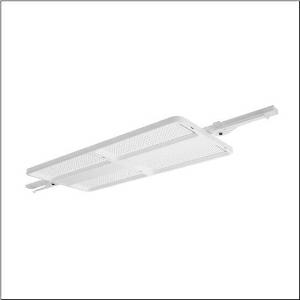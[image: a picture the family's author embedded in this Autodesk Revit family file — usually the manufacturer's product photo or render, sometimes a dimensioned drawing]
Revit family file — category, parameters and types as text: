
# Revit family: highbay_11_fur_modario_r__tragschiene_maxi_51hn11db4rma_e5d8
name_source: partatom
category: Lighting Fixtures
units: mm (PartAtom-declared; Revit-internal decimal feet)

## family parameters
Cut with Voids When Loaded = No
Host = Face
Light Source = No
Part Type = Normal
Room Calculation Point = No
Round Connector Dimension = Use Diameter
Shared = No

## types (1)
- --- (1 x LED, 42500 lm, 213.7 W, 4000K)
    Apparent Load = 214 VA
    CIE Flux Codes = 85 97 100 100 100
    Color Rendering = 80
    Color Temperature = 4000K
    Default Elevation = 1800 mm
    Description = high bay luminaire Highbay 11 for Modario® trunking rail maxi; direct symmetric narrow distribution, light control with lens of PMMA; UGR ≤ 22 (X = 4H | Y = 8H | S = 0.25H | reflection values 70/50/20); luminous flux: 42.500lm; light colour: 840, colour temperature: 4000K, MacAdam ≤ 2 SDCM (initial), colour rendering: CRI > 80; luminous efficacy: 198,9lm/W; rated service life: 100.000h (L95/B50) at AT= 25°C; control: DALI 2; luminaire connection: plug, 5-pole, with phase selectionmains connection: 230..240V, AC 50/60Hz; connected load: 213,7W; protection rating (complete): IP64; insulation class (complete): insulation class I (protective earthing); protection symbol: D; impact resistance: IK07; certification: CE, ENEC, VDE, UKCA; internal wiring halogen-free; luminaire LABS conformity tested according to VDMA 24364:2018-05; corresponds to IFS (International Featured Standards) requirements for safety and quality in the food industry; housing frame of high-performance plastic PA6, matt traffic white (RAL 9016); cover of PMMA; fixing on rail side of steel, galvanised, white; blank cover of PC, traffic white (RAL 9016); dimension (LxWxH): 1.496 x 442 x 72mm; permissible operating ambient temperature: -40..+50°C (reducing of maximum allowable ambient temperature of 5°C with ceiling mounting); packaging unit: 1 piece
    Height = 72 mm  [stored 0.23622 ft]
    Lamp = 1 x LED
    Lamp Light Flux = 42500 lm
    Lamp Power = 213.7 W
    Lamp count = 1
    Length = 946 mm
    Luminous efficacy = 199 lm/W
    Manufacturer = Siteco
    ModVariant = No
    Model = 51HN11DB4RMA
    Mounting Place = Ceiling
    Mounting Type = Pendant
    Number of Poles = 1
    OnlyDefault = Yes
    Power Factor = 1
    Product Name = Highbay 11 für Modario® Tragschiene maxi
    Product group = high bay luminaire
    ProductGroupID = 901
    Protection Class = Protection class I
    Protection Degree = IP 64
    RLX_Detail_Level = 1
    RLX_Emergency_Light_Flux = 0 lm
    RLX_Emergency_Type = 0
    RLX_Emergency_Type_DB = No
    RlxData = <blob elided: 21425 chars, md5=75a6247b>
    Socket = socket
    Standby Power = 0 W
    System Light Flux = 42501 lm
    System Power = 214 W
    Type Comments = factory setting: luminous flux: 100 % | dim-lin: 254 | 983 mA
    Type Image = l_1363248.jpg
    URL = http://relux.com
    VarID = @adj_013267
    Voltage = 0 V
    Weight = 0.00 kg
    Width = 442 mm

note: [stored X ft] marks values corroborated as IEEE doubles in the binary element streams (Revit-internal decimal feet)

## geometry (parser evidence)
native form markers: Blend x4, Sweep x11
no freeform markers — native parametric forms only
